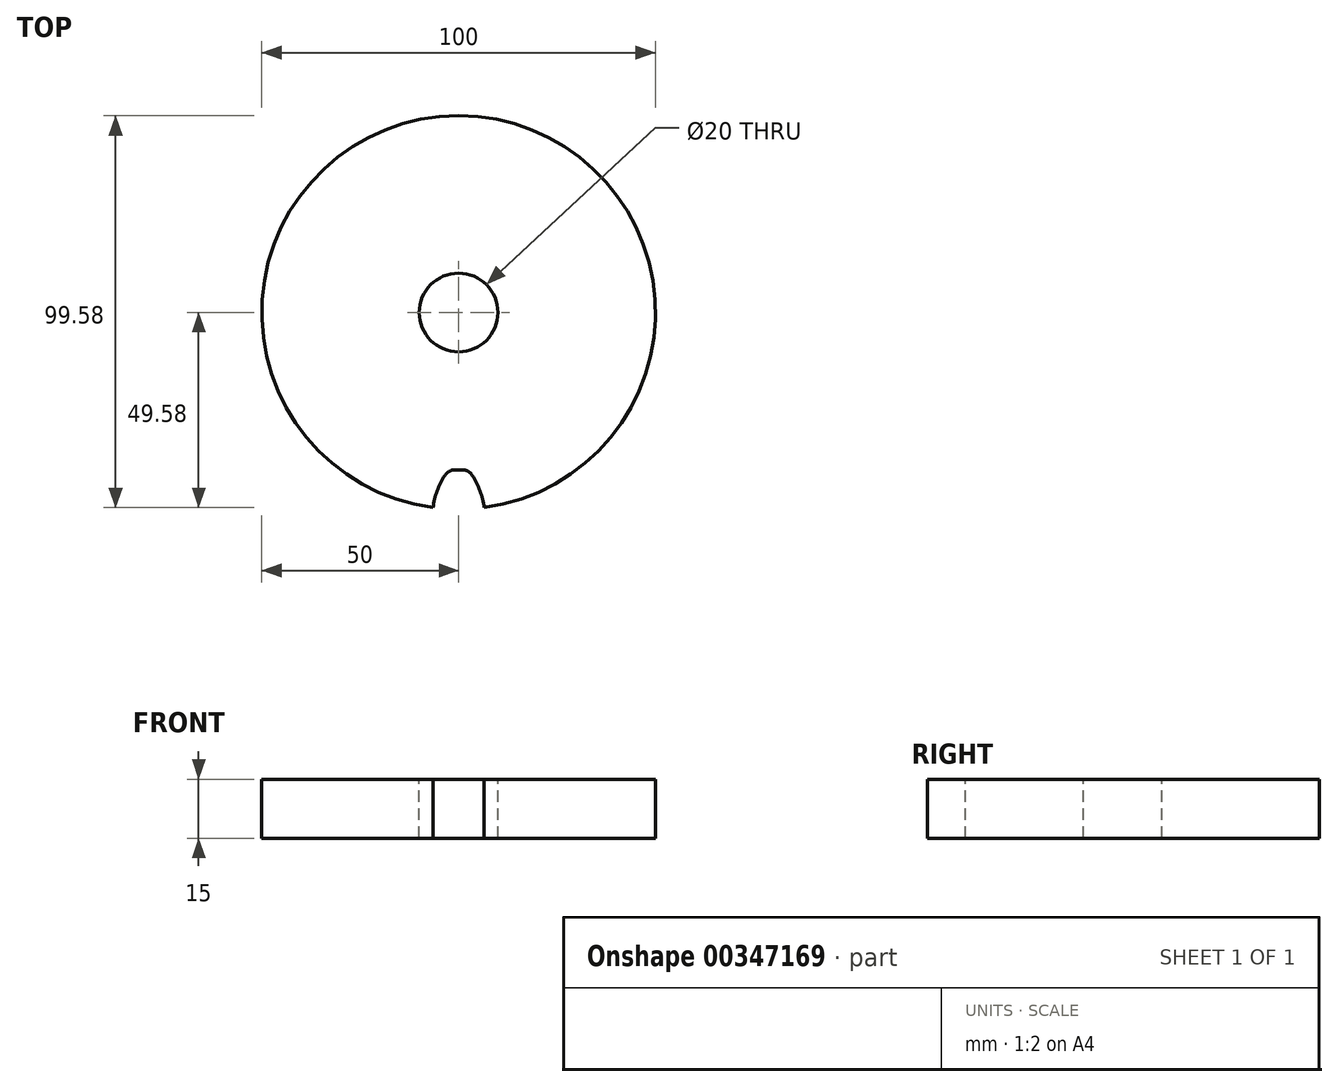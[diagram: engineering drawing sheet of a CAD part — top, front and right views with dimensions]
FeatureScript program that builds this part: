
annotation { "Feature Type Name" : "Feature", "Feature Type Description" : "" }
export const myFeature = defineFeature(function(context is Context, id is Id, definition is map)
    precondition{}
    {
        {
            var Q0;
            Q0=qCreatedBy(makeId("Top.planeOp"),FACE);
            var sketch = newSketch(context, id + "F0", { "sketchPlane" : qUnion([Q0])});
            skCircle(sketch, "E0", {"center": v(0, 0) * mm, "radius": 50 * mm});
            skSolve(sketch);
        }
        {
            var Q0;
            Q0 = qSketchRegion(id + "F0", true);
            extrude(context, id + "F1", {"entities" : qUnion([Q0]), "depth" : 15 * mm});
        }
        {
            var Q0;
            Q0=makeQuery(id+"F1.opExtrude","CAP_FACE",FACE,{"disambiguationData":[OSD([sQuery(id+"F0.wireOp",EDGE,"E0")])],"isStart":false});
            var sketch = newSketch(context, id + "F2", { "sketchPlane" : qUnion([Q0])});
            skLineSegment(sketch, "E1", {"start": v(0, 0) * mm, "end": v(0, -56.03) * mm, "construction": true});
            skArc(sketch, "E2", {"start": v(6.5, -49.58) * mm, "mid": v(5.44, -45.3) * mm, "end": v(3.47, -41.37) * mm});
            skLineSegment(sketch, "E3", {"start": v(0.95, -40) * mm, "end": v(-0.95, -40) * mm});
            skCircle(sketch, "E4", {"center": v(0, 0) * mm, "radius": 40 * mm, "construction": true});
            skArc(sketch, "E5.MirrorCS", {"start": v(-6.5, -49.58) * mm, "mid": v(-5.44, -45.3) * mm, "end": v(-3.47, -41.37) * mm});
            skPoint(sketch, "E6.visualSharp", {"position": v(2.5, -40) * mm});
            skArc(sketch, "E6.filletArc", {"start": v(3.47, -41.37) * mm, "mid": v(2.39, -40.36) * mm, "end": v(0.95, -40) * mm});
            skPoint(sketch, "E7.visualSharp", {"position": v(-2.5, -40) * mm});
            skArc(sketch, "E7.filletArc", {"start": v(-0.95, -40) * mm, "mid": v(-2.39, -40.36) * mm, "end": v(-3.47, -41.37) * mm});
            skCircle(sketch, "E8.0", {"center": v(0, 0) * mm, "radius": 50 * mm});
            skSolve(sketch);
        }
        {
            var Q0;
            Q0=makeQuery(id+"F2.imprint","IMPRINT",FACE,{"disambiguationData":[TD([[makeQuery(id+"F2.imprint","IMPRINT",EDGE,{"derivedFrom":sQuery(id+"F2.wireOp",EDGE,"E2")}),1.0]])]});
            extrude(context, id + "F3", {"entities" : qUnion([Q0]), "operationType" : NewBodyOperationType.REMOVE, "oppositeDirection" : true, "depth" : 25 * mm});
        }
        {
            var Q0;
            Q0=makeQuery(id+"FrWebrpohlywjBq_1.12.F3.boolean.opBoolean","COPY",EDGE,{"derivedFrom":makeQuery(id+"FrWebrpohlywjBq_1.12.F3.opExtrude","SWEPT_EDGE",EDGE,{"disambiguationData":[OSD([sQuery(id+"F0.wireOp",EDGE,"E0"),sQuery(id+"F2.wireOp",EDGE,"E2"),sQuery(id+"F2.wireOp",EDGE,"63738e59-9a88-4130-a17f-bf0dbf4aad581")])]})});
            var Q1;
            Q1=makeQuery(id+"FrWebrpohlywjBq_1.11.F3.boolean.opBoolean","COPY",EDGE,{"derivedFrom":makeQuery(id+"FrWebrpohlywjBq_1.11.F3.opExtrude","SWEPT_EDGE",EDGE,{"disambiguationData":[OSD([sQuery(id+"F0.wireOp",EDGE,"E0"),sQuery(id+"F2.wireOp",EDGE,"E5.MirrorCS"),sQuery(id+"F2.wireOp",EDGE,"63738e59-9a88-4130-a17f-bf0dbf4aad581")])]})});
            var Q2;
            Q2=makeQuery(id+"FrWebrpohlywjBq_1.11.F3.boolean.opBoolean","COPY",EDGE,{"derivedFrom":makeQuery(id+"FrWebrpohlywjBq_1.11.F3.opExtrude","SWEPT_EDGE",EDGE,{"disambiguationData":[OSD([sQuery(id+"F0.wireOp",EDGE,"E0"),sQuery(id+"F2.wireOp",EDGE,"E2"),sQuery(id+"F2.wireOp",EDGE,"63738e59-9a88-4130-a17f-bf0dbf4aad581")])]})});
            var Q3;
            Q3=makeQuery(id+"FrWebrpohlywjBq_1.10.F3.boolean.opBoolean","COPY",EDGE,{"derivedFrom":makeQuery(id+"FrWebrpohlywjBq_1.10.F3.opExtrude","SWEPT_EDGE",EDGE,{"disambiguationData":[OSD([sQuery(id+"F0.wireOp",EDGE,"E0"),sQuery(id+"F2.wireOp",EDGE,"E5.MirrorCS"),sQuery(id+"F2.wireOp",EDGE,"63738e59-9a88-4130-a17f-bf0dbf4aad581")])]})});
            var Q4;
            Q4=makeQuery(id+"FrWebrpohlywjBq_1.10.F3.boolean.opBoolean","COPY",EDGE,{"derivedFrom":makeQuery(id+"FrWebrpohlywjBq_1.10.F3.opExtrude","SWEPT_EDGE",EDGE,{"disambiguationData":[OSD([sQuery(id+"F0.wireOp",EDGE,"E0"),sQuery(id+"F2.wireOp",EDGE,"E2"),sQuery(id+"F2.wireOp",EDGE,"63738e59-9a88-4130-a17f-bf0dbf4aad581")])]})});
            var Q5;
            Q5=makeQuery(id+"FrWebrpohlywjBq_1.9.F3.boolean.opBoolean","COPY",EDGE,{"derivedFrom":makeQuery(id+"FrWebrpohlywjBq_1.9.F3.opExtrude","SWEPT_EDGE",EDGE,{"disambiguationData":[OSD([sQuery(id+"F0.wireOp",EDGE,"E0"),sQuery(id+"F2.wireOp",EDGE,"E5.MirrorCS"),sQuery(id+"F2.wireOp",EDGE,"63738e59-9a88-4130-a17f-bf0dbf4aad581")])]})});
            var Q6;
            Q6=makeQuery(id+"FrWebrpohlywjBq_1.9.F3.boolean.opBoolean","COPY",EDGE,{"derivedFrom":makeQuery(id+"FrWebrpohlywjBq_1.9.F3.opExtrude","SWEPT_EDGE",EDGE,{"disambiguationData":[OSD([sQuery(id+"F0.wireOp",EDGE,"E0"),sQuery(id+"F2.wireOp",EDGE,"E2"),sQuery(id+"F2.wireOp",EDGE,"63738e59-9a88-4130-a17f-bf0dbf4aad581")])]})});
            var Q7;
            Q7=makeQuery(id+"FrWebrpohlywjBq_1.8.F3.boolean.opBoolean","COPY",EDGE,{"derivedFrom":makeQuery(id+"FrWebrpohlywjBq_1.8.F3.opExtrude","SWEPT_EDGE",EDGE,{"disambiguationData":[OSD([sQuery(id+"F0.wireOp",EDGE,"E0"),sQuery(id+"F2.wireOp",EDGE,"E5.MirrorCS"),sQuery(id+"F2.wireOp",EDGE,"63738e59-9a88-4130-a17f-bf0dbf4aad581")])]})});
            var Q8;
            Q8=makeQuery(id+"FrWebrpohlywjBq_1.8.F3.boolean.opBoolean","COPY",EDGE,{"derivedFrom":makeQuery(id+"FrWebrpohlywjBq_1.8.F3.opExtrude","SWEPT_EDGE",EDGE,{"disambiguationData":[OSD([sQuery(id+"F0.wireOp",EDGE,"E0"),sQuery(id+"F2.wireOp",EDGE,"E2"),sQuery(id+"F2.wireOp",EDGE,"63738e59-9a88-4130-a17f-bf0dbf4aad581")])]})});
            var Q9;
            Q9=makeQuery(id+"FrWebrpohlywjBq_1.7.F3.boolean.opBoolean","COPY",EDGE,{"derivedFrom":makeQuery(id+"FrWebrpohlywjBq_1.7.F3.opExtrude","SWEPT_EDGE",EDGE,{"disambiguationData":[OSD([sQuery(id+"F0.wireOp",EDGE,"E0"),sQuery(id+"F2.wireOp",EDGE,"E5.MirrorCS"),sQuery(id+"F2.wireOp",EDGE,"63738e59-9a88-4130-a17f-bf0dbf4aad581")])]})});
            var Q10;
            Q10=makeQuery(id+"FrWebrpohlywjBq_1.7.F3.boolean.opBoolean","COPY",EDGE,{"derivedFrom":makeQuery(id+"FrWebrpohlywjBq_1.7.F3.opExtrude","SWEPT_EDGE",EDGE,{"disambiguationData":[OSD([sQuery(id+"F0.wireOp",EDGE,"E0"),sQuery(id+"F2.wireOp",EDGE,"E2"),sQuery(id+"F2.wireOp",EDGE,"63738e59-9a88-4130-a17f-bf0dbf4aad581")])]})});
            var Q11;
            Q11=makeQuery(id+"FrWebrpohlywjBq_1.6.F3.boolean.opBoolean","COPY",EDGE,{"derivedFrom":makeQuery(id+"FrWebrpohlywjBq_1.6.F3.opExtrude","SWEPT_EDGE",EDGE,{"disambiguationData":[OSD([sQuery(id+"F0.wireOp",EDGE,"E0"),sQuery(id+"F2.wireOp",EDGE,"E5.MirrorCS"),sQuery(id+"F2.wireOp",EDGE,"63738e59-9a88-4130-a17f-bf0dbf4aad581")])]})});
            var Q12;
            Q12=makeQuery(id+"FrWebrpohlywjBq_1.6.F3.boolean.opBoolean","COPY",EDGE,{"derivedFrom":makeQuery(id+"FrWebrpohlywjBq_1.6.F3.opExtrude","SWEPT_EDGE",EDGE,{"disambiguationData":[OSD([sQuery(id+"F0.wireOp",EDGE,"E0"),sQuery(id+"F2.wireOp",EDGE,"E2"),sQuery(id+"F2.wireOp",EDGE,"63738e59-9a88-4130-a17f-bf0dbf4aad581")])]})});
            var Q13;
            Q13=makeQuery(id+"FrWebrpohlywjBq_1.5.F3.boolean.opBoolean","COPY",EDGE,{"derivedFrom":makeQuery(id+"FrWebrpohlywjBq_1.5.F3.opExtrude","SWEPT_EDGE",EDGE,{"disambiguationData":[OSD([sQuery(id+"F0.wireOp",EDGE,"E0"),sQuery(id+"F2.wireOp",EDGE,"E5.MirrorCS"),sQuery(id+"F2.wireOp",EDGE,"63738e59-9a88-4130-a17f-bf0dbf4aad581")])]})});
            var Q14;
            Q14=makeQuery(id+"FrWebrpohlywjBq_1.5.F3.boolean.opBoolean","COPY",EDGE,{"derivedFrom":makeQuery(id+"FrWebrpohlywjBq_1.5.F3.opExtrude","SWEPT_EDGE",EDGE,{"disambiguationData":[OSD([sQuery(id+"F0.wireOp",EDGE,"E0"),sQuery(id+"F2.wireOp",EDGE,"E2"),sQuery(id+"F2.wireOp",EDGE,"63738e59-9a88-4130-a17f-bf0dbf4aad581")])]})});
            var Q15;
            Q15=makeQuery(id+"FrWebrpohlywjBq_1.4.F3.boolean.opBoolean","COPY",EDGE,{"derivedFrom":makeQuery(id+"FrWebrpohlywjBq_1.4.F3.opExtrude","SWEPT_EDGE",EDGE,{"disambiguationData":[OSD([sQuery(id+"F0.wireOp",EDGE,"E0"),sQuery(id+"F2.wireOp",EDGE,"E5.MirrorCS"),sQuery(id+"F2.wireOp",EDGE,"63738e59-9a88-4130-a17f-bf0dbf4aad581")])]})});
            var Q16;
            Q16=makeQuery(id+"FrWebrpohlywjBq_1.4.F3.boolean.opBoolean","COPY",EDGE,{"derivedFrom":makeQuery(id+"FrWebrpohlywjBq_1.4.F3.opExtrude","SWEPT_EDGE",EDGE,{"disambiguationData":[OSD([sQuery(id+"F0.wireOp",EDGE,"E0"),sQuery(id+"F2.wireOp",EDGE,"E2"),sQuery(id+"F2.wireOp",EDGE,"63738e59-9a88-4130-a17f-bf0dbf4aad581")])]})});
            var Q17;
            Q17=makeQuery(id+"FrWebrpohlywjBq_1.3.F3.boolean.opBoolean","COPY",EDGE,{"derivedFrom":makeQuery(id+"FrWebrpohlywjBq_1.3.F3.opExtrude","SWEPT_EDGE",EDGE,{"disambiguationData":[OSD([sQuery(id+"F0.wireOp",EDGE,"E0"),sQuery(id+"F2.wireOp",EDGE,"E5.MirrorCS"),sQuery(id+"F2.wireOp",EDGE,"63738e59-9a88-4130-a17f-bf0dbf4aad581")])]})});
            var Q18;
            Q18=makeQuery(id+"FrWebrpohlywjBq_1.3.F3.boolean.opBoolean","COPY",EDGE,{"derivedFrom":makeQuery(id+"FrWebrpohlywjBq_1.3.F3.opExtrude","SWEPT_EDGE",EDGE,{"disambiguationData":[OSD([sQuery(id+"F0.wireOp",EDGE,"E0"),sQuery(id+"F2.wireOp",EDGE,"E2"),sQuery(id+"F2.wireOp",EDGE,"63738e59-9a88-4130-a17f-bf0dbf4aad581")])]})});
            var Q19;
            Q19=makeQuery(id+"FrWebrpohlywjBq_1.2.F3.boolean.opBoolean","COPY",EDGE,{"derivedFrom":makeQuery(id+"FrWebrpohlywjBq_1.2.F3.opExtrude","SWEPT_EDGE",EDGE,{"disambiguationData":[OSD([sQuery(id+"F0.wireOp",EDGE,"E0"),sQuery(id+"F2.wireOp",EDGE,"E5.MirrorCS"),sQuery(id+"F2.wireOp",EDGE,"63738e59-9a88-4130-a17f-bf0dbf4aad581")])]})});
            var Q20;
            Q20=makeQuery(id+"FrWebrpohlywjBq_1.2.F3.boolean.opBoolean","COPY",EDGE,{"derivedFrom":makeQuery(id+"FrWebrpohlywjBq_1.2.F3.opExtrude","SWEPT_EDGE",EDGE,{"disambiguationData":[OSD([sQuery(id+"F0.wireOp",EDGE,"E0"),sQuery(id+"F2.wireOp",EDGE,"E2"),sQuery(id+"F2.wireOp",EDGE,"63738e59-9a88-4130-a17f-bf0dbf4aad581")])]})});
            var Q21;
            Q21=makeQuery(id+"FrWebrpohlywjBq_1.1.F3.boolean.opBoolean","COPY",EDGE,{"derivedFrom":makeQuery(id+"FrWebrpohlywjBq_1.1.F3.opExtrude","SWEPT_EDGE",EDGE,{"disambiguationData":[OSD([sQuery(id+"F0.wireOp",EDGE,"E0"),sQuery(id+"F2.wireOp",EDGE,"E5.MirrorCS"),sQuery(id+"F2.wireOp",EDGE,"63738e59-9a88-4130-a17f-bf0dbf4aad581")])]})});
            var Q22;
            Q22=makeQuery(id+"FrWebrpohlywjBq_1.1.F3.boolean.opBoolean","COPY",EDGE,{"derivedFrom":makeQuery(id+"FrWebrpohlywjBq_1.1.F3.opExtrude","SWEPT_EDGE",EDGE,{"disambiguationData":[OSD([sQuery(id+"F0.wireOp",EDGE,"E0"),sQuery(id+"F2.wireOp",EDGE,"E2"),sQuery(id+"F2.wireOp",EDGE,"63738e59-9a88-4130-a17f-bf0dbf4aad581")])]})});
            var Q23;
            Q23=makeQuery(id+"F3.boolean.opBoolean","COPY",EDGE,{"derivedFrom":makeQuery(id+"F3.opExtrude","SWEPT_EDGE",EDGE,{"disambiguationData":[OSD([sQuery(id+"F0.wireOp",EDGE,"E0"),sQuery(id+"F2.wireOp",EDGE,"E5.MirrorCS"),sQuery(id+"F2.wireOp",EDGE,"63738e59-9a88-4130-a17f-bf0dbf4aad581")])]})});
            var Q24;
            Q24=makeQuery(id+"F3.boolean.opBoolean","COPY",EDGE,{"derivedFrom":makeQuery(id+"F3.opExtrude","SWEPT_EDGE",EDGE,{"disambiguationData":[OSD([sQuery(id+"F0.wireOp",EDGE,"E0"),sQuery(id+"F2.wireOp",EDGE,"E2"),sQuery(id+"F2.wireOp",EDGE,"63738e59-9a88-4130-a17f-bf0dbf4aad581")])]})});
            var Q25;
            Q25=makeQuery(id+"FrWebrpohlywjBq_1.14.F3.boolean.opBoolean","COPY",EDGE,{"derivedFrom":makeQuery(id+"FrWebrpohlywjBq_1.14.F3.opExtrude","SWEPT_EDGE",EDGE,{"disambiguationData":[OSD([sQuery(id+"F0.wireOp",EDGE,"E0"),sQuery(id+"F2.wireOp",EDGE,"E5.MirrorCS"),sQuery(id+"F2.wireOp",EDGE,"63738e59-9a88-4130-a17f-bf0dbf4aad581")])]})});
            var Q26;
            Q26=makeQuery(id+"FrWebrpohlywjBq_1.14.F3.boolean.opBoolean","COPY",EDGE,{"derivedFrom":makeQuery(id+"FrWebrpohlywjBq_1.14.F3.opExtrude","SWEPT_EDGE",EDGE,{"disambiguationData":[OSD([sQuery(id+"F0.wireOp",EDGE,"E0"),sQuery(id+"F2.wireOp",EDGE,"E2"),sQuery(id+"F2.wireOp",EDGE,"63738e59-9a88-4130-a17f-bf0dbf4aad581")])]})});
            var Q27;
            Q27=makeQuery(id+"FrWebrpohlywjBq_1.13.F3.boolean.opBoolean","COPY",EDGE,{"derivedFrom":makeQuery(id+"FrWebrpohlywjBq_1.13.F3.opExtrude","SWEPT_EDGE",EDGE,{"disambiguationData":[OSD([sQuery(id+"F0.wireOp",EDGE,"E0"),sQuery(id+"F2.wireOp",EDGE,"E5.MirrorCS"),sQuery(id+"F2.wireOp",EDGE,"63738e59-9a88-4130-a17f-bf0dbf4aad581")])]})});
            var Q28;
            Q28=makeQuery(id+"FrWebrpohlywjBq_1.13.F3.boolean.opBoolean","COPY",EDGE,{"derivedFrom":makeQuery(id+"FrWebrpohlywjBq_1.13.F3.opExtrude","SWEPT_EDGE",EDGE,{"disambiguationData":[OSD([sQuery(id+"F0.wireOp",EDGE,"E0"),sQuery(id+"F2.wireOp",EDGE,"E2"),sQuery(id+"F2.wireOp",EDGE,"63738e59-9a88-4130-a17f-bf0dbf4aad581")])]})});
            var Q29;
            Q29=makeQuery(id+"FrWebrpohlywjBq_1.12.F3.boolean.opBoolean","COPY",EDGE,{"derivedFrom":makeQuery(id+"FrWebrpohlywjBq_1.12.F3.opExtrude","SWEPT_EDGE",EDGE,{"disambiguationData":[OSD([sQuery(id+"F0.wireOp",EDGE,"E0"),sQuery(id+"F2.wireOp",EDGE,"E5.MirrorCS"),sQuery(id+"F2.wireOp",EDGE,"63738e59-9a88-4130-a17f-bf0dbf4aad581")])]})});
            fillet(context, id + "F4", {"entities" : qUnion([Q0, Q1, Q2, Q3, Q4, Q5, Q6, Q7, Q8, Q9, Q10, Q11, Q12, Q13, Q14, Q15, Q16, Q17, Q18, Q19, Q20, Q21, Q22, Q23, Q24, Q25, Q26, Q27, Q28, Q29]), "radius" : 3 * mm, "tangentPropagation" : true, "allowEdgeOverflow" : false});
        }
        {
            var Q0;
            Q0=makeQuery(id+"F1.opExtrude","CAP_FACE",FACE,{"disambiguationData":[OSD([sQuery(id+"F0.wireOp",EDGE,"E0")])],"isStart":false});
            var sketch = newSketch(context, id + "F5", { "sketchPlane" : qUnion([Q0])});
            skCircle(sketch, "E9", {"center": v(0, 0) * mm, "radius": 10 * mm});
            skSolve(sketch);
        }
        {
            var Q0;
            Q0=makeQuery(id+"F5.imprint","IMPRINT",FACE,{"disambiguationData":[TD([[makeQuery(id+"F5.imprint","IMPRINT",EDGE,{"derivedFrom":sQuery(id+"F5.wireOp",EDGE,"E9")}),1.0]])]});
            extrude(context, id + "F6", {"entities" : qUnion([Q0]), "operationType" : NewBodyOperationType.REMOVE, "oppositeDirection" : true, "depth" : 25 * mm});
        }
    });
